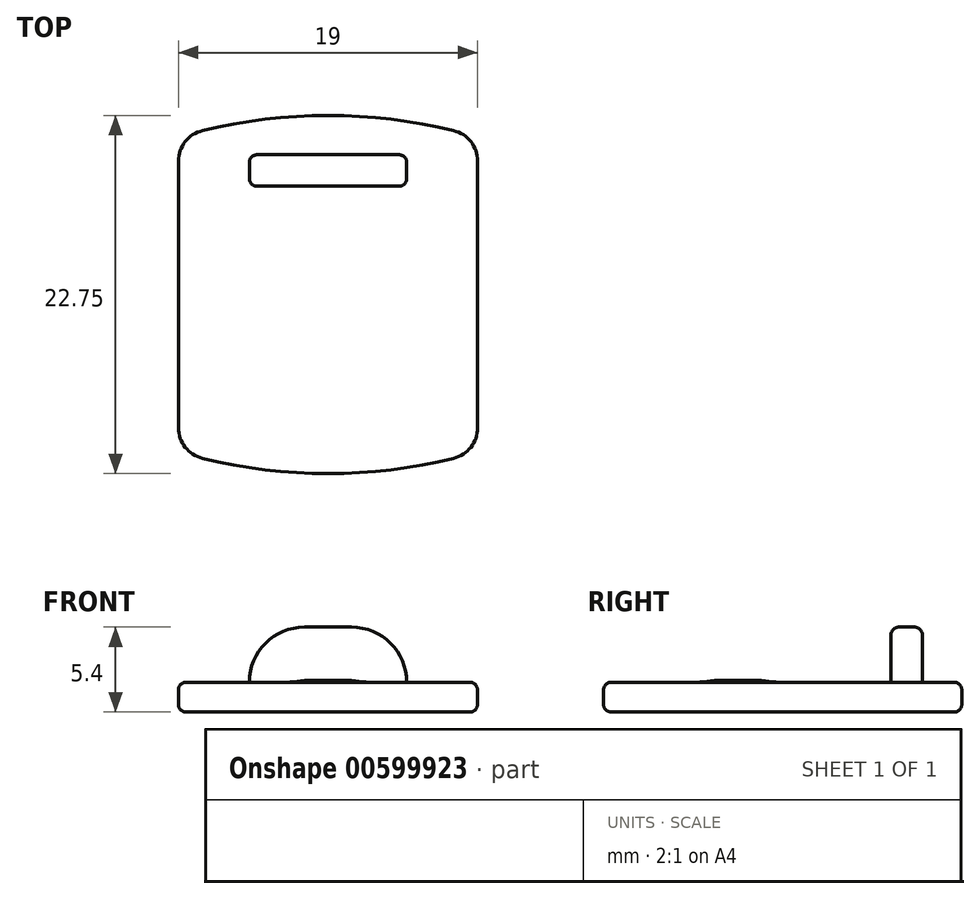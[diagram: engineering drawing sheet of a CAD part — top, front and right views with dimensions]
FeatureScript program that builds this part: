
annotation { "Feature Type Name" : "Feature", "Feature Type Description" : "" }
export const myFeature = defineFeature(function(context is Context, id is Id, definition is map)
    precondition{}
    {
        {
            var Q0;
            Q0=qCreatedBy(makeId("Top.planeOp"),FACE);
            var sketch = newSketch(context, id + "F0", { "sketchPlane" : qUnion([Q0])});
            skArc(sketch, "E0.0", {"start": v(9.5, 32.12) * mm, "mid": v(0, 33.5) * mm, "end": v(-9.5, 32.12) * mm});
            skLineSegment(sketch, "E1", {"start": v(-9.5, 32.12) * mm, "end": v(-9.5, 12.12) * mm});
            skLineSegment(sketch, "E2", {"start": v(9.5, 32.12) * mm, "end": v(9.5, 12.12) * mm});
            skArc(sketch, "E3.MirrorCS", {"start": v(9.5, 12.12) * mm, "mid": v(0, 10.75) * mm, "end": v(-9.5, 12.12) * mm});
            skSolve(sketch);
        }
        {
            var Q0;
            Q0 = qSketchRegion(id + "F0", true);
            extrude(context, id + "F1", {"entities" : qUnion([Q0]), "depth" : 1.9 * mm, "offsetDistance" : 25 * mm});
        }
        {
            var Q0;
            Q0=makeQuery(id+"F1.opExtrude","CAP_FACE",FACE,{"disambiguationData":[OSD([sQuery(id+"F0.wireOp",EDGE,"E0.0"),sQuery(id+"F0.wireOp",EDGE,"E1"),sQuery(id+"F0.wireOp",EDGE,"E2"),sQuery(id+"F0.wireOp",EDGE,"E3.MirrorCS")])],"isStart":false});
            var sketch = newSketch(context, id + "F2", { "sketchPlane" : qUnion([Q0])});
            skLineSegment(sketch, "E4", {"start": v(-5, 31) * mm, "end": v(5, 31) * mm});
            skLineSegment(sketch, "E5", {"start": v(-5, 31) * mm, "end": v(-5, 29) * mm});
            skLineSegment(sketch, "E6", {"start": v(-5, 29) * mm, "end": v(5, 29) * mm});
            skLineSegment(sketch, "E7", {"start": v(5, 29) * mm, "end": v(5, 31) * mm});
            skSolve(sketch);
        }
        {
            var Q0;
            Q0 = qSketchRegion(id + "F2", true);
            extrude(context, id + "F3", {"entities" : qUnion([Q0]), "operationType" : NewBodyOperationType.ADD, "depth" : 3.5 * mm, "offsetDistance" : 25 * mm});
        }
        {
            var Q0;
            Q0=makeQuery(id+"F3.opExtrude","CAP_EDGE",EDGE,{"disambiguationData":[OSD([sQuery(id+"F2.wireOp",EDGE,"E7")])],"isStart":false});
            var Q1;
            Q1=makeQuery(id+"F3.opExtrude","CAP_EDGE",EDGE,{"disambiguationData":[OSD([sQuery(id+"F2.wireOp",EDGE,"E5")])],"isStart":false});
            fillet(context, id + "F4", {"entities" : qUnion([Q0, Q1]), "radius" : 3.5 * mm, "tangentPropagation" : true, "allowEdgeOverflow" : false});
        }
        {
            var Q0;
            Q0=makeQuery(id+"F3.opExtrude","CAP_EDGE",EDGE,{"disambiguationData":[OSD([sQuery(id+"F2.wireOp",EDGE,"E6")])],"isStart":false});
            var Q1;
            Q1=makeQuery(id+"F3.opExtrude","CAP_FACE",FACE,{"disambiguationData":[OSD([sQuery(id+"F2.wireOp",EDGE,"E4"),sQuery(id+"F2.wireOp",EDGE,"E5"),sQuery(id+"F2.wireOp",EDGE,"E6"),sQuery(id+"F2.wireOp",EDGE,"E7")])],"isStart":false});
            fillet(context, id + "F5", {"entities" : qUnion([Q0, Q1]), "radius" : .5 * mm, "tangentPropagation" : true, "allowEdgeOverflow" : false});
        }
        {
            var Q0;
            Q0=makeQuery(id+"F3.opExtrude","CAP_EDGE",EDGE,{"disambiguationData":[OSD([sQuery(id+"F2.wireOp",EDGE,"E6")])],"isStart":true});
            var Q1;
            Q1=makeQuery(id+"F1.opExtrude","SWEPT_EDGE",EDGE,{"disambiguationData":[OSD([sQuery(id+"F0.wireOp",EDGE,"E1"),sQuery(id+"F0.wireOp",EDGE,"E3.MirrorCS")])]});
            var Q2;
            Q2=makeQuery(id+"F1.opExtrude","SWEPT_EDGE",EDGE,{"disambiguationData":[OSD([sQuery(id+"F0.wireOp",EDGE,"E0.0"),sQuery(id+"F0.wireOp",EDGE,"E1")])]});
            var Q3;
            Q3=makeQuery(id+"F1.opExtrude","SWEPT_EDGE",EDGE,{"disambiguationData":[OSD([sQuery(id+"F0.wireOp",EDGE,"E2"),sQuery(id+"F0.wireOp",EDGE,"E3.MirrorCS")])]});
            var Q4;
            Q4=makeQuery(id+"F1.opExtrude","SWEPT_EDGE",EDGE,{"disambiguationData":[OSD([sQuery(id+"F0.wireOp",EDGE,"E0.0"),sQuery(id+"F0.wireOp",EDGE,"E2")])]});
            fillet(context, id + "F6", {"entities" : qUnion([Q0, Q1, Q2, Q3, Q4]), "radius" : 2 * mm, "tangentPropagation" : true, "allowEdgeOverflow" : false});
        }
        {
            var Q0;
            Q0=makeQuery(id+"F1.opExtrude","CAP_EDGE",EDGE,{"disambiguationData":[OSD([sQuery(id+"F0.wireOp",EDGE,"E3.MirrorCS")])],"isStart":false});
            var Q1;
            Q1=makeQuery(id+"F1.opExtrude","CAP_EDGE",EDGE,{"disambiguationData":[OSD([sQuery(id+"F0.wireOp",EDGE,"E3.MirrorCS")])],"isStart":true});
            fillet(context, id + "F7", {"entities" : qUnion([Q0, Q1]), "radius" : .5 * mm, "tangentPropagation" : true, "allowEdgeOverflow" : false});
        }
        {
            var Q0;
            Q0=makeQuery(id+"F7.opFillet","SPLIT",FACE,{"disambiguationData":[OD(1.0)],"derivedFrom":makeQuery(id+"F1.opExtrude","CAP_FACE",FACE,{"disambiguationData":[OSD([sQuery(id+"F0.wireOp",EDGE,"E0.0"),sQuery(id+"F0.wireOp",EDGE,"E1"),sQuery(id+"F0.wireOp",EDGE,"E2"),sQuery(id+"F0.wireOp",EDGE,"E3.MirrorCS")])],"isStart":false})});
            var sketch = newSketch(context, id + "F8", { "sketchPlane" : qUnion([Q0])});
            skCircle(sketch, "E8", {"center": v(0, 19.29) * mm, "radius": 2 * mm});
            skSolve(sketch);
        }
        {
            var Q0;
            Q0 = qSketchRegion(id + "F8", true);
            extrude(context, id + "F9", {"entities" : qUnion([Q0]), "operationType" : NewBodyOperationType.ADD, "depth" : .1 * mm, "offsetDistance" : 25 * mm});
        }
        {
            var Q0;
            Q0=makeQuery(id+"F9.opExtrude","CAP_EDGE",EDGE,{"disambiguationData":[OSD([sQuery(id+"F8.wireOp",EDGE,"E8")])],"isStart":false});
            fillet(context, id + "F10", {"entities" : qUnion([Q0]), "radius" : 2 * mm, "tangentPropagation" : true, "allowEdgeOverflow" : false});
        }
        {
            var Q0;
            Q0=makeQuery(id+"F10.opFillet","BLEND_EDGE",EDGE,{"blendedFrom":[makeQuery(id+"F9.opExtrude","CAP_EDGE",EDGE,{"disambiguationData":[OSD([sQuery(id+"F8.wireOp",EDGE,"E8")])],"isStart":false}),makeQuery(id+"F7.opFillet","SPLIT",FACE,{"disambiguationData":[OD(1.0)],"derivedFrom":makeQuery(id+"F1.opExtrude","CAP_FACE",FACE,{"disambiguationData":[OSD([sQuery(id+"F0.wireOp",EDGE,"E0.0"),sQuery(id+"F0.wireOp",EDGE,"E1"),sQuery(id+"F0.wireOp",EDGE,"E2"),sQuery(id+"F0.wireOp",EDGE,"E3.MirrorCS")])],"isStart":false})})],"blendedInto":[makeQuery(id+"F7.opFillet","SPLIT",FACE,{"disambiguationData":[OD(1.0)],"derivedFrom":makeQuery(id+"F1.opExtrude","CAP_FACE",FACE,{"disambiguationData":[OSD([sQuery(id+"F0.wireOp",EDGE,"E0.0"),sQuery(id+"F0.wireOp",EDGE,"E1"),sQuery(id+"F0.wireOp",EDGE,"E2"),sQuery(id+"F0.wireOp",EDGE,"E3.MirrorCS")])],"isStart":false})})]});
            fillet(context, id + "F11", {"entities" : qUnion([Q0]), "radius" : 5 * mm, "tangentPropagation" : true, "allowEdgeOverflow" : false});
        }
    });
